# Revit family: Infire_Inside C version 3
name_source: partatom
category: Zabudowa
revit_build: Autodesk Revit 2018 (Build: 20170223_1515(x64)
units: mm (PartAtom-declared; Revit-internal decimal feet)

## family parameters
Numer OmniClass = 23.40.20.34.14
Obiekt nadrzędny = Powierzchnia
Punkt obliczania pomieszczeń = Nie
Tnij formami wycięć po wczytaniu = Nie
Tytuł OmniClass = Fireplaces
Współdzielony = Nie

## types (2) — shared parameters
Domyślna rzędna = 1000 mm  [stored 3.28084 ft]
Gwarancja = 24 miesiące
Głębokość = 300 mm
IfcExportAs = IfcSpaceHeaterType
Komentarze do typu = Biokominek
Materiał (obudowa) = INFIRE - czarny
Materiał (szkło) = INFIRE - szkło
Model = INSIDE C1000/C1200 vers3
Obraz typu = Infire_Inside C1000 v3.jpg
Producent = INFIRE Biokominki
Szkło = Szyba hartowana 4 mm, przyciemniana
URL = http://www.infire.pl
Wysokość = 500 mm  [stored 1.64042 ft]
Wysokość szyby = 150 mm

## per-type parameters (varying)
| type | Szerokość | Szerokość szyby |
| INSIDE C1000 version 3 | 1000 mm  [stored 3.28084 ft] | 945 mm |
| INSIDE C1200 version 3 | 1200 mm | 1145 mm |

note: [stored X ft] marks values corroborated as IEEE doubles in the binary element streams (Revit-internal decimal feet)
